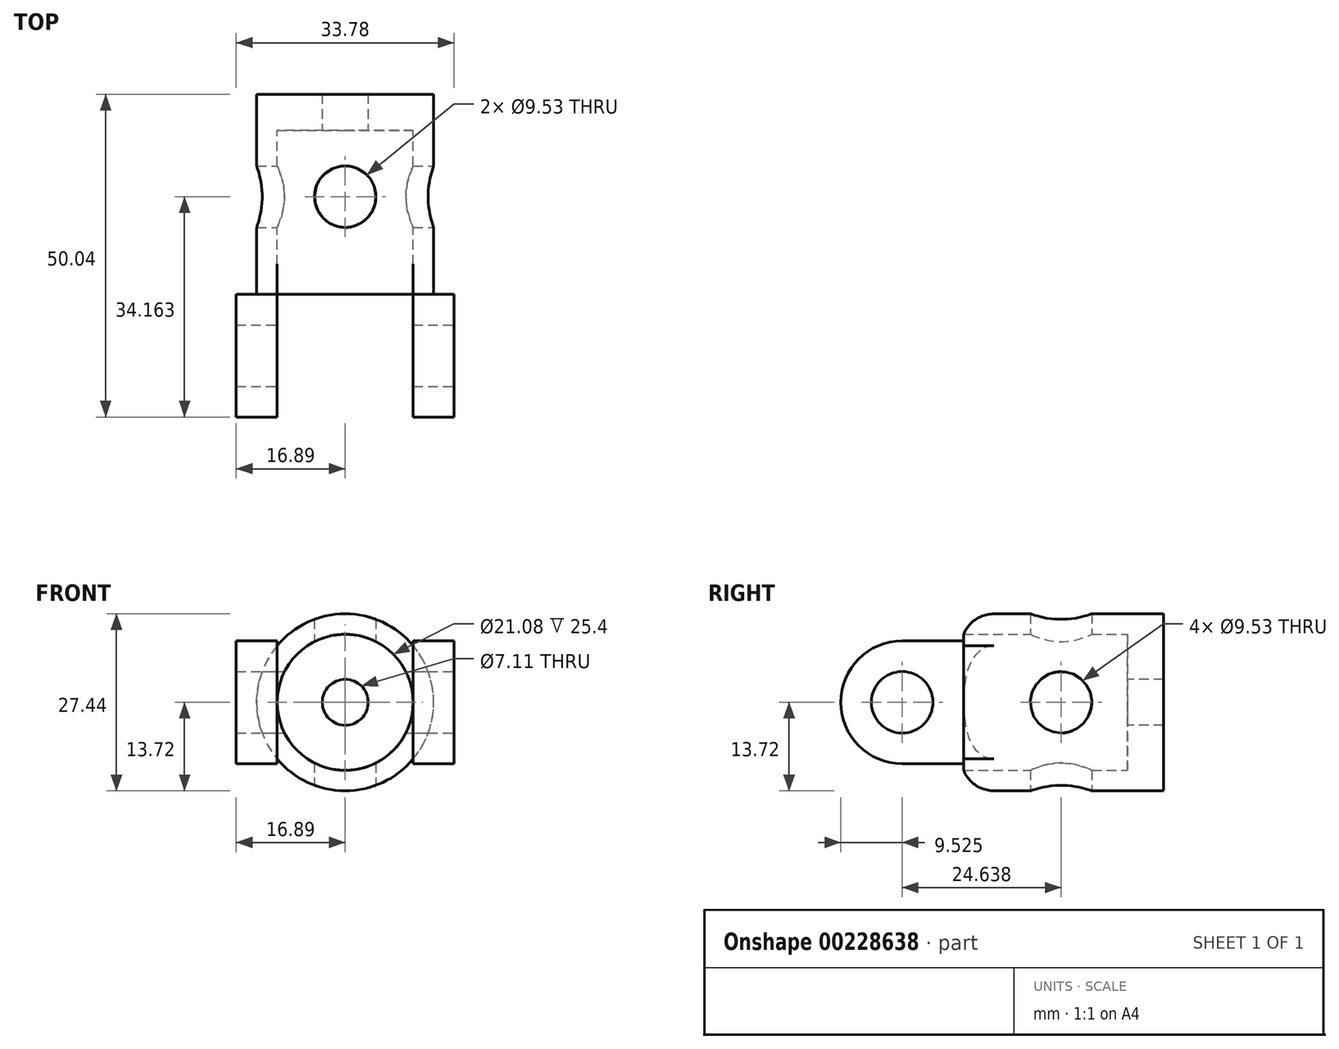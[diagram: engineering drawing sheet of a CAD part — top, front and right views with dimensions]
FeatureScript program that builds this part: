
annotation { "Feature Type Name" : "Feature", "Feature Type Description" : "" }
export const myFeature = defineFeature(function(context is Context, id is Id, definition is map)
    precondition{}
    {
        {
            var Q0;
            Q0=qCreatedBy(makeId("Front.planeOp"),FACE);
            var sketch = newSketch(context, id + "F0", { "sketchPlane" : qUnion([Q0])});
            skCircle(sketch, "E0", {"center": v(0, 0) * mm, "radius": 13.72 * mm});
            skCircle(sketch, "E1", {"center": v(0, 0) * mm, "radius": 10.54 * mm});
            skSolve(sketch);
        }
        {
            var Q0;
            Q0 = qSketchRegion(id + "F0", true);
            extrude(context, id + "F1", {"entities" : qUnion([Q0]), "depth" : 25.4 * mm, "offsetDistance" : 25.4 * mm});
        }
        {
            var Q0;
            Q0=makeQuery(id+"F1.opExtrude","CAP_FACE",FACE,{"disambiguationData":[OSD([sQuery(id+"F0.wireOp",EDGE,"E0"),sQuery(id+"F0.wireOp",EDGE,"E1")])],"isStart":true});
            var sketch = newSketch(context, id + "F2", { "sketchPlane" : qUnion([Q0])});
            skCircle(sketch, "E2", {"center": v(0, 0) * mm, "radius": 13.72 * mm});
            skCircle(sketch, "E3", {"center": v(0, 0) * mm, "radius": 3.56 * mm});
            skSolve(sketch);
        }
        {
            var Q0;
            Q0 = qSketchRegion(id + "F2", true);
            extrude(context, id + "F3", {"entities" : qUnion([Q0]), "operationType" : NewBodyOperationType.ADD, "depth" : 5.6 * mm, "offsetDistance" : 25.4 * mm});
        }
        {
            var Q0;
            Q0=qCreatedBy(makeId("Top.planeOp"),FACE);
            var sketch = newSketch(context, id + "F4", { "sketchPlane" : qUnion([Q0])});
            skCircle(sketch, "E4", {"center": v(0, -10.29) * mm, "radius": 4.76 * mm});
            skSolve(sketch);
        }
        {
            var Q0;
            Q0 = qSketchRegion(id + "F4", true);
            extrude(context, id + "F5", {"entities" : qUnion([Q0]), "operationType" : NewBodyOperationType.REMOVE, "depth" : 25.4 * mm, "offsetDistance" : 25.4 * mm, "hasSecondDirection" : true, "secondDirectionOppositeDirection" : true, "secondDirectionDepth" : 25.4 * mm});
        }
        {
            var Q0;
            Q0=qCreatedBy(makeId("Right.planeOp"),FACE);
            var sketch = newSketch(context, id + "F6", { "sketchPlane" : qUnion([Q0])});
            skCircle(sketch, "E5", {"center": v(-10.29, 0) * mm, "radius": 4.76 * mm});
            skSolve(sketch);
        }
        {
            var Q0;
            Q0 = qSketchRegion(id + "F6", true);
            extrude(context, id + "F7", {"entities" : qUnion([Q0]), "operationType" : NewBodyOperationType.REMOVE, "oppositeDirection" : true, "depth" : 25.4 * mm, "offsetDistance" : 25.4 * mm, "hasSecondDirection" : true, "secondDirectionOppositeDirection" : false, "secondDirectionDepth" : 25.4 * mm});
        }
        {
            var Q0;
            Q0=makeQuery(id+"F1.opExtrude","CAP_FACE",FACE,{"disambiguationData":[OSD([sQuery(id+"F0.wireOp",EDGE,"E0"),sQuery(id+"F0.wireOp",EDGE,"E1")])],"isStart":false});
            var sketch = newSketch(context, id + "F8", { "sketchPlane" : qUnion([Q0])});
            skLineSegment(sketch, "E6.bottom", {"start": v(10.54, 9.53) * mm, "end": v(16.9, 9.53) * mm});
            skLineSegment(sketch, "E6.top", {"start": v(10.54, -9.53) * mm, "end": v(16.9, -9.53) * mm});
            skLineSegment(sketch, "E6.left", {"start": v(10.54, 9.53) * mm, "end": v(10.54, -9.53) * mm});
            skLineSegment(sketch, "E6.right", {"start": v(16.9, 9.53) * mm, "end": v(16.9, -9.53) * mm});
            skLineSegment(sketch, "E7.bottom", {"start": v(-16.9, 9.53) * mm, "end": v(-10.54, 9.53) * mm});
            skLineSegment(sketch, "E7.top", {"start": v(-16.9, -9.53) * mm, "end": v(-10.54, -9.53) * mm});
            skLineSegment(sketch, "E7.left", {"start": v(-16.9, 9.53) * mm, "end": v(-16.9, -9.53) * mm});
            skLineSegment(sketch, "E7.right", {"start": v(-10.54, 9.53) * mm, "end": v(-10.54, -9.53) * mm});
            skSolve(sketch);
        }
        {
            var Q0;
            Q0 = qSketchRegion(id + "F8", true);
            extrude(context, id + "F9", {"entities" : qUnion([Q0]), "operationType" : NewBodyOperationType.ADD, "depth" : 19.05 * mm, "offsetDistance" : 25.4 * mm});
        }
        {
            var Q0;
            {var subQ0=sQuery(id+"F0.wireOp",EDGE,"E0");Q0=makeQuery(id+"F9.boolean.opBoolean","SPLIT",EDGE,{"disambiguationData":[topologyDisambiguationEdgeConnected([makeQuery(id+"F1.opExtrude","SWEPT_FACE",FACE,{"disambiguationData":[OSD([subQ0])]}),makeQuery(id+"F3.opExtrude","SWEPT_FACE",FACE,{"disambiguationData":[OSD([sQuery(id+"F2.wireOp",EDGE,"E2")])]}),makeQuery(id+"F9.opExtrude","CAP_FACE",FACE,{"disambiguationData":[OSD([sQuery(id+"F8.wireOp",EDGE,"E7.bottom"),sQuery(id+"F8.wireOp",EDGE,"E7.top"),sQuery(id+"F8.wireOp",EDGE,"E7.left"),sQuery(id+"F8.wireOp",EDGE,"E7.right")])],"isStart":true})])],"derivedFrom":makeQuery(id+"F1.opExtrude","CAP_EDGE",EDGE,{"disambiguationData":[OSD([subQ0])],"isStart":false})});}
            var Q1;
            {var subQ0=sQuery(id+"F0.wireOp",EDGE,"E0");Q1=makeQuery(id+"F9.boolean.opBoolean","SPLIT",EDGE,{"disambiguationData":[topologyDisambiguationEdgeConnected([makeQuery(id+"F1.opExtrude","SWEPT_FACE",FACE,{"disambiguationData":[OSD([subQ0])]}),makeQuery(id+"F3.opExtrude","SWEPT_FACE",FACE,{"disambiguationData":[OSD([sQuery(id+"F2.wireOp",EDGE,"E2")])]}),makeQuery(id+"F9.opExtrude","CAP_FACE",FACE,{"disambiguationData":[OSD([sQuery(id+"F8.wireOp",EDGE,"E6.bottom"),sQuery(id+"F8.wireOp",EDGE,"E6.top"),sQuery(id+"F8.wireOp",EDGE,"E6.left"),sQuery(id+"F8.wireOp",EDGE,"E6.right")])],"isStart":true})])],"derivedFrom":makeQuery(id+"F1.opExtrude","CAP_EDGE",EDGE,{"disambiguationData":[OSD([subQ0])],"isStart":false})});}
            fillet(context, id + "F10", {"entities" : qUnion([Q0, Q1]), "radius" : 5.08 * mm, "tangentPropagation" : true, "allowEdgeOverflow" : false});
        }
        {
            var Q0;
            Q0=makeQuery(id+"F9.opExtrude","CAP_EDGE",EDGE,{"disambiguationData":[OSD([sQuery(id+"F8.wireOp",EDGE,"E7.bottom")])],"isStart":false});
            var Q1;
            Q1=makeQuery(id+"F9.opExtrude","CAP_EDGE",EDGE,{"disambiguationData":[OSD([sQuery(id+"F8.wireOp",EDGE,"E7.top")])],"isStart":false});
            var Q2;
            Q2=makeQuery(id+"F9.opExtrude","CAP_EDGE",EDGE,{"disambiguationData":[OSD([sQuery(id+"F8.wireOp",EDGE,"E6.bottom")])],"isStart":false});
            var Q3;
            Q3=makeQuery(id+"F9.opExtrude","CAP_EDGE",EDGE,{"disambiguationData":[OSD([sQuery(id+"F8.wireOp",EDGE,"E6.top")])],"isStart":false});
            fillet(context, id + "F11", {"entities" : qUnion([Q0, Q1, Q2, Q3]), "radius" : 9.52 * mm, "tangentPropagation" : true, "allowEdgeOverflow" : false});
        }
        {
            var Q0;
            Q0=makeQuery(id+"F9.opExtrude","SWEPT_FACE",FACE,{"disambiguationData":[OSD([sQuery(id+"F8.wireOp",EDGE,"E6.right")])]});
            var sketch = newSketch(context, id + "F12", { "sketchPlane" : qUnion([Q0])});
            skCircle(sketch, "E8", {"center": v(-34.93, 0) * mm, "radius": 4.76 * mm});
            skSolve(sketch);
        }
        {
            var Q0;
            Q0 = qSketchRegion(id + "F12", true);
            extrude(context, id + "F13", {"entities" : qUnion([Q0]), "operationType" : NewBodyOperationType.REMOVE, "endBound" : BoundingType.THROUGH_ALL, "oppositeDirection" : true, "depth" : 25.4 * mm, "offsetDistance" : 25.4 * mm});
        }
    });
